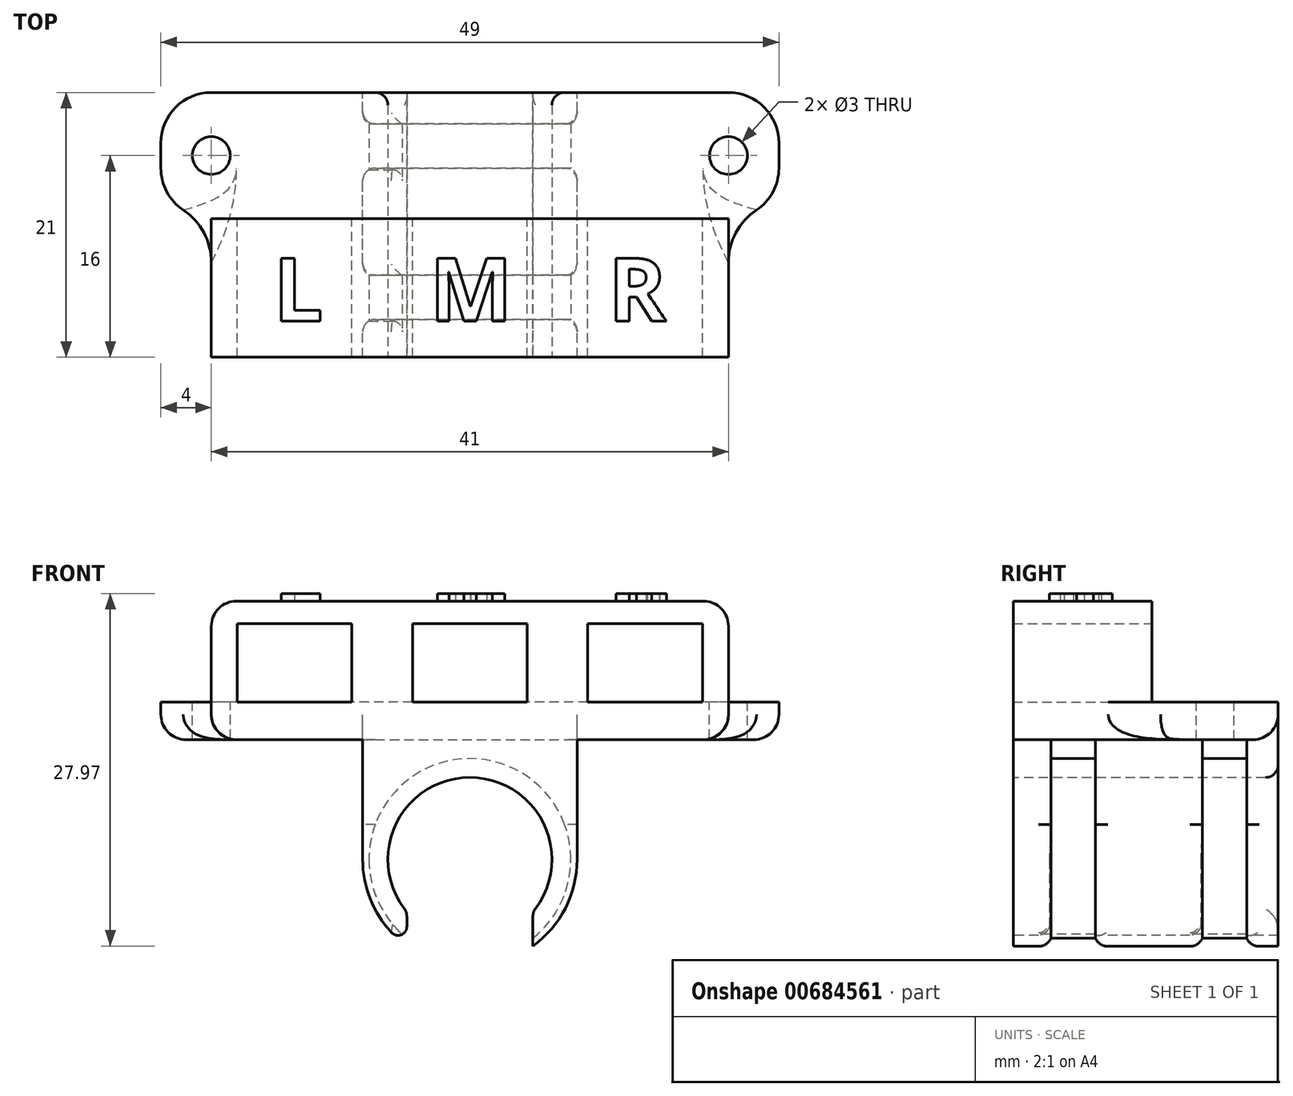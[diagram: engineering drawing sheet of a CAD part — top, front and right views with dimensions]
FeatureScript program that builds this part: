
annotation { "Feature Type Name" : "Feature", "Feature Type Description" : "" }
export const myFeature = defineFeature(function(context is Context, id is Id, definition is map)
    precondition{}
    {
        {
            var Q0;
            Q0=qCreatedBy(makeId("Front.planeOp"),FACE);
            var sketch = newSketch(context, id + "F0", { "sketchPlane" : qUnion([Q0])});
            skLineSegment(sketch, "E0.bottom", {"start": v(0, 0) * mm, "end": v(41, 0) * mm});
            skLineSegment(sketch, "E0.top", {"start": v(0, 11) * mm, "end": v(41, 11) * mm});
            skLineSegment(sketch, "E0.left", {"start": v(0, 0) * mm, "end": v(0, 11) * mm});
            skLineSegment(sketch, "E0.right", {"start": v(41, 0) * mm, "end": v(41, 11) * mm});
            skSolve(sketch);
        }
        {
            var Q0;
            Q0=makeQuery(id+"F0.imprint","IMPRINT",FACE,{"disambiguationData":[TD([[makeQuery(id+"F0.imprint","IMPRINT",EDGE,{"derivedFrom":sQuery(id+"F0.wireOp",EDGE,"E0.bottom")}),1.0]])]});
            extrude(context, id + "F1", {"entities" : qUnion([Q0]), "depth" : 11 * mm});
        }
        {
            var Q0;
            Q0=makeQuery(id+"F1.opExtrude","CAP_FACE",FACE,{"disambiguationData":[OSD([sQuery(id+"F0.wireOp",EDGE,"E0.bottom"),sQuery(id+"F0.wireOp",EDGE,"E0.top"),sQuery(id+"F0.wireOp",EDGE,"E0.left"),sQuery(id+"F0.wireOp",EDGE,"E0.right")])],"isStart":true});
            var sketch = newSketch(context, id + "F2", { "sketchPlane" : qUnion([Q0])});
            skLineSegment(sketch, "E1.bottom", {"start": v(-41, 0) * mm, "end": v(0, 0) * mm});
            skLineSegment(sketch, "E1.top", {"start": v(-41, 3) * mm, "end": v(0, 3) * mm});
            skLineSegment(sketch, "E1.left", {"start": v(-41, 0) * mm, "end": v(-41, 3) * mm});
            skLineSegment(sketch, "E1.right", {"start": v(0, 0) * mm, "end": v(0, 3) * mm});
            skSolve(sketch);
        }
        {
            var Q0;
            Q0=makeQuery(id+"F2.imprint","IMPRINT",FACE,{"disambiguationData":[TD([[makeQuery(id+"F2.imprint","IMPRINT",EDGE,{"derivedFrom":sQuery(id+"F2.wireOp",EDGE,"E1.bottom")}),-1.0]])]});
            extrude(context, id + "F3", {"entities" : qUnion([Q0]), "operationType" : NewBodyOperationType.ADD, "depth" : 10 * mm});
        }
        {
            var Q0;
            Q0=makeQuery(id+"F1.opExtrude","CAP_FACE",FACE,{"disambiguationData":[OSD([sQuery(id+"F0.wireOp",EDGE,"E0.bottom"),sQuery(id+"F0.wireOp",EDGE,"E0.top"),sQuery(id+"F0.wireOp",EDGE,"E0.left"),sQuery(id+"F0.wireOp",EDGE,"E0.right")])],"isStart":true});
            var sketch = newSketch(context, id + "F4", { "sketchPlane" : qUnion([Q0])});
            skLineSegment(sketch, "E2.bottom", {"start": v(-38.95, 3) * mm, "end": v(-29.85, 3) * mm});
            skLineSegment(sketch, "E2.top", {"start": v(-38.95, 9.2) * mm, "end": v(-29.85, 9.2) * mm});
            skLineSegment(sketch, "E2.left", {"start": v(-38.95, 3) * mm, "end": v(-38.95, 9.2) * mm});
            skLineSegment(sketch, "E2.right", {"start": v(-29.85, 3) * mm, "end": v(-29.85, 9.2) * mm});
            skLineSegment(sketch, "E3.bottom", {"start": v(-25.05, 3) * mm, "end": v(-15.95, 3) * mm});
            skLineSegment(sketch, "E3.top", {"start": v(-25.05, 9.2) * mm, "end": v(-15.95, 9.2) * mm});
            skLineSegment(sketch, "E3.left", {"start": v(-25.05, 3) * mm, "end": v(-25.05, 9.2) * mm});
            skLineSegment(sketch, "E3.right", {"start": v(-15.95, 3) * mm, "end": v(-15.95, 9.2) * mm});
            skLineSegment(sketch, "E4.bottom", {"start": v(-11.15, 3) * mm, "end": v(-2.05, 3) * mm});
            skLineSegment(sketch, "E4.top", {"start": v(-11.15, 9.2) * mm, "end": v(-2.05, 9.2) * mm});
            skLineSegment(sketch, "E4.left", {"start": v(-11.15, 3) * mm, "end": v(-11.15, 9.2) * mm});
            skLineSegment(sketch, "E4.right", {"start": v(-2.05, 3) * mm, "end": v(-2.05, 9.2) * mm});
            skSolve(sketch);
        }
        {
            var Q0;
            Q0=makeQuery(id+"F4.imprint","IMPRINT",FACE,{"disambiguationData":[TD([[makeQuery(id+"F4.imprint","IMPRINT",EDGE,{"derivedFrom":sQuery(id+"F4.wireOp",EDGE,"E2.bottom")}),1.0]])]});
            var Q1;
            Q1=makeQuery(id+"F4.imprint","IMPRINT",FACE,{"disambiguationData":[TD([[makeQuery(id+"F4.imprint","IMPRINT",EDGE,{"derivedFrom":sQuery(id+"F4.wireOp",EDGE,"E3.bottom")}),1.0]])]});
            var Q2;
            Q2=makeQuery(id+"F4.imprint","IMPRINT",FACE,{"disambiguationData":[TD([[makeQuery(id+"F4.imprint","IMPRINT",EDGE,{"derivedFrom":sQuery(id+"F4.wireOp",EDGE,"E4.bottom")}),1.0]])]});
            extrude(context, id + "F5", {"entities" : qUnion([Q0, Q1, Q2]), "operationType" : NewBodyOperationType.REMOVE, "endBound" : BoundingType.THROUGH_ALL, "oppositeDirection" : true, "depth" : 25 * mm});
        }
        {
            var Q0;
            Q0=makeQuery(id+"F3.boolean.opBoolean","MERGE",FACE,{"derivedFrom":[makeQuery(id+"F1.opExtrude","SWEPT_FACE",FACE,{"disambiguationData":[OSD([sQuery(id+"F0.wireOp",EDGE,"E0.bottom")])]}),makeQuery(id+"F3.opExtrude","SWEPT_FACE",FACE,{"disambiguationData":[OSD([sQuery(id+"F2.wireOp",EDGE,"E1.bottom")])]})]});
            var sketch = newSketch(context, id + "F6", { "sketchPlane" : qUnion([Q0])});
            skLineSegment(sketch, "E5.bottom", {"start": v(12, 11) * mm, "end": v(29, 11) * mm});
            skLineSegment(sketch, "E5.top", {"start": v(12, -10) * mm, "end": v(29, -10) * mm});
            skLineSegment(sketch, "E5.left", {"start": v(12, 11) * mm, "end": v(12, -10) * mm});
            skLineSegment(sketch, "E5.right", {"start": v(29, 11) * mm, "end": v(29, -10) * mm});
            skSolve(sketch);
        }
        {
            var Q0;
            Q0=makeQuery(id+"F6.imprint","IMPRINT",FACE,{"disambiguationData":[TD([[makeQuery(id+"F6.imprint","IMPRINT",EDGE,{"derivedFrom":sQuery(id+"F6.wireOp",EDGE,"E5.bottom")}),-1.0]])]});
            extrude(context, id + "F7", {"entities" : qUnion([Q0]), "operationType" : NewBodyOperationType.ADD, "depth" : 18 * mm});
        }
        {
            var Q0;
            Q0=makeQuery(id+"F7.opExtrude","CAP_EDGE",EDGE,{"disambiguationData":[OSD([sQuery(id+"F6.wireOp",EDGE,"E5.left")])],"isStart":false});
            var Q1;
            Q1=makeQuery(id+"F7.opExtrude","CAP_EDGE",EDGE,{"disambiguationData":[OSD([sQuery(id+"F6.wireOp",EDGE,"E5.right")])],"isStart":false});
            fillet(context, id + "F8", {"entities" : qUnion([Q0, Q1]), "radius" : 8.5 * mm, "tangentPropagation" : true, "allowEdgeOverflow" : false});
        }
        {
            var Q0;
            Q0=makeQuery(id+"F7.boolean.opBoolean","MERGE",FACE,{"derivedFrom":[makeQuery(id+"F1.opExtrude","CAP_FACE",FACE,{"disambiguationData":[OSD([sQuery(id+"F0.wireOp",EDGE,"E0.bottom"),sQuery(id+"F0.wireOp",EDGE,"E0.top"),sQuery(id+"F0.wireOp",EDGE,"E0.left"),sQuery(id+"F0.wireOp",EDGE,"E0.right")])],"isStart":false}),makeQuery(id+"F7.opExtrude","SWEPT_FACE",FACE,{"disambiguationData":[OSD([sQuery(id+"F6.wireOp",EDGE,"E5.bottom")])]})]});
            var sketch = newSketch(context, id + "F9", { "sketchPlane" : qUnion([Q0])});
            skCircle(sketch, "E6", {"center": v(20.5, -9.5) * mm, "radius": 6.5 * mm});
            skLineSegment(sketch, "E7.bottom", {"start": v(15.5, -10.8) * mm, "end": v(25.5, -10.8) * mm});
            skLineSegment(sketch, "E7.top", {"start": v(15.5, -21.95) * mm, "end": v(25.5, -21.95) * mm});
            skLineSegment(sketch, "E7.left", {"start": v(15.5, -10.8) * mm, "end": v(15.5, -21.95) * mm});
            skLineSegment(sketch, "E7.right", {"start": v(25.5, -10.8) * mm, "end": v(25.5, -21.95) * mm});
            skSolve(sketch);
        }
        {
            var Q0;
            {var subQ5=sQuery(id+"F9.wireOp",EDGE,"E7.bottom");Q0=makeQuery(id+"F9.imprint","IMPRINT",FACE,{"disambiguationData":[TD([[makeQuery(id+"F9.imprint","IMPRINT",EDGE,{"derivedFrom":subQ5}),1.0]])]});}
            var Q1;
            {var subQ5=sQuery(id+"F9.wireOp",EDGE,"E7.bottom");Q1=makeQuery(id+"F9.imprint","IMPRINT",FACE,{"disambiguationData":[TD([[makeQuery(id+"F9.imprint","IMPRINT",EDGE,{"derivedFrom":subQ5}),-1.0]])]});}
            var Q2;
            {var subQ0=sQuery(id+"F9.wireOp",EDGE,"E7.left");var subQ1=sQuery(id+"F9.wireOp",EDGE,"E6");var subQ2=makeQuery(id+"F9.imprint","INTERSECT",VERTEX,{"derivedFrom":[subQ1,subQ0]});Q2=makeQuery(id+"F9.imprint","IMPRINT",FACE,{"disambiguationData":[TD([[makeQuery(id+"F9.imprint","IMPRINT",EDGE,{"disambiguationData":[TD([[subQ2,-1.0]])],"derivedFrom":subQ1}),-1.0]])]});}
            extrude(context, id + "F10", {"entities" : qUnion([Q0, Q1, Q2]), "operationType" : NewBodyOperationType.REMOVE, "endBound" : BoundingType.THROUGH_ALL, "oppositeDirection" : true, "depth" : 25 * mm});
        }
        {
            var Q0;
            Q0=makeQuery(id+"F10.boolean.opBoolean","COPY",EDGE,{"derivedFrom":makeQuery(id+"F10.opExtrude","SWEPT_EDGE",EDGE,{"disambiguationData":[OSD([sQuery(id+"F0.wireOp",EDGE,"E0.bottom"),sQuery(id+"F0.wireOp",EDGE,"E0.top"),sQuery(id+"F0.wireOp",EDGE,"E0.left"),sQuery(id+"F0.wireOp",EDGE,"E0.right"),sQuery(id+"F6.wireOp",EDGE,"E5.bottom"),sQuery(id+"F6.wireOp",EDGE,"E5.right"),sQuery(id+"F9.wireOp",EDGE,"E7.left")])]})});
            var Q1;
            Q1=makeQuery(id+"F10.boolean.opBoolean","COPY",EDGE,{"derivedFrom":makeQuery(id+"F10.opExtrude","SWEPT_EDGE",EDGE,{"disambiguationData":[OSD([sQuery(id+"F0.wireOp",EDGE,"E0.bottom"),sQuery(id+"F0.wireOp",EDGE,"E0.top"),sQuery(id+"F0.wireOp",EDGE,"E0.left"),sQuery(id+"F0.wireOp",EDGE,"E0.right"),sQuery(id+"F6.wireOp",EDGE,"E5.bottom"),sQuery(id+"F6.wireOp",EDGE,"E5.right"),sQuery(id+"F9.wireOp",EDGE,"E7.right")])]})});
            fillet(context, id + "F11", {"entities" : qUnion([Q0, Q1]), "radius" : 0.7 * mm, "tangentPropagation" : true, "allowEdgeOverflow" : false});
        }
        {
            var Q0;
            Q0=qCreatedBy(makeId("Front.planeOp"),FACE);
            cPlane(context, id + "F12", {"entities" : qUnion([Q0]), "cplaneType" : CPlaneType.OFFSET, "offset" : 4 * mm, "oppositeDirection" : true, "width" : 150 * mm, "height" : 150 * mm});
        }
        {
            var Q0;
            Q0=qCreatedBy(makeId("Front.planeOp"),FACE);
            cPlane(context, id + "F13", {"entities" : qUnion([Q0]), "cplaneType" : CPlaneType.OFFSET, "offset" : 8 * mm, "width" : 150 * mm, "height" : 150 * mm});
        }
        {
            var Q0;
            Q0=qCreatedBy(id+"F13.planeOp",FACE);
            var sketch = newSketch(context, id + "F14", { "sketchPlane" : qUnion([Q0])});
            skLineSegment(sketch, "E8.bottom", {"start": v(0, 0) * mm, "end": v(41, 0) * mm});
            skLineSegment(sketch, "E8.top", {"start": v(0, -18) * mm, "end": v(41, -18) * mm});
            skLineSegment(sketch, "E8.left", {"start": v(0, 0) * mm, "end": v(0, -18) * mm});
            skLineSegment(sketch, "E8.right", {"start": v(41, 0) * mm, "end": v(41, -18) * mm});
            skCircle(sketch, "E9", {"center": v(20.5, -9.5) * mm, "radius": 8 * mm});
            skSolve(sketch);
        }
        {
            var Q0;
            Q0=makeQuery(id+"F14.imprint","IMPRINT",FACE,{"disambiguationData":[TD([[makeQuery(id+"F14.imprint","IMPRINT",EDGE,{"derivedFrom":sQuery(id+"F14.wireOp",EDGE,"E8.bottom")}),-1.0]])]});
            extrude(context, id + "F15", {"entities" : qUnion([Q0]), "operationType" : NewBodyOperationType.REMOVE, "oppositeDirection" : true, "depth" : 3.5 * mm});
        }
        {
            var Q0;
            Q0=qCreatedBy(id+"F12.planeOp",FACE);
            var sketch = newSketch(context, id + "F16", { "sketchPlane" : qUnion([Q0])});
            skLineSegment(sketch, "E10.bottom", {"start": v(0, 0) * mm, "end": v(41, 0) * mm});
            skLineSegment(sketch, "E10.top", {"start": v(0, -18) * mm, "end": v(41, -18) * mm});
            skLineSegment(sketch, "E10.left", {"start": v(0, 0) * mm, "end": v(0, -18) * mm});
            skLineSegment(sketch, "E10.right", {"start": v(41, 0) * mm, "end": v(41, -18) * mm});
            skCircle(sketch, "E11", {"center": v(20.5, -9.5) * mm, "radius": 8 * mm});
            skSolve(sketch);
        }
        {
            var Q0;
            Q0=makeQuery(id+"F16.imprint","IMPRINT",FACE,{"disambiguationData":[TD([[makeQuery(id+"F16.imprint","IMPRINT",EDGE,{"derivedFrom":sQuery(id+"F16.wireOp",EDGE,"E10.bottom")}),-1.0]])]});
            extrude(context, id + "F17", {"entities" : qUnion([Q0]), "operationType" : NewBodyOperationType.REMOVE, "oppositeDirection" : true, "depth" : 3.5 * mm});
        }
        {
            var Q0;
            Q0=makeQuery(id+"F15.boolean.opBoolean","INTERSECT",EDGE,{"derivedFrom":[makeQuery(id+"F7.opExtrude","SWEPT_FACE",FACE,{"disambiguationData":[OSD([sQuery(id+"F6.wireOp",EDGE,"E5.right")])]}),makeQuery(id+"F15.opExtrude","CAP_FACE",FACE,{"disambiguationData":[OSD([sQuery(id+"F14.wireOp",EDGE,"E8.bottom"),sQuery(id+"F14.wireOp",EDGE,"E8.top"),sQuery(id+"F14.wireOp",EDGE,"E8.left"),sQuery(id+"F14.wireOp",EDGE,"E8.right"),sQuery(id+"F14.wireOp",EDGE,"E9")])],"isStart":true})]});
            var Q1;
            Q1=makeQuery(id+"F15.boolean.opBoolean","INTERSECT",EDGE,{"derivedFrom":[makeQuery(id+"F7.opExtrude","SWEPT_FACE",FACE,{"disambiguationData":[OSD([sQuery(id+"F6.wireOp",EDGE,"E5.right")])]}),makeQuery(id+"F15.opExtrude","CAP_FACE",FACE,{"disambiguationData":[OSD([sQuery(id+"F14.wireOp",EDGE,"E8.bottom"),sQuery(id+"F14.wireOp",EDGE,"E8.top"),sQuery(id+"F14.wireOp",EDGE,"E8.left"),sQuery(id+"F14.wireOp",EDGE,"E8.right"),sQuery(id+"F14.wireOp",EDGE,"E9")])],"isStart":false})]});
            var Q2;
            {var subQ1=sQuery(id+"F6.wireOp",EDGE,"E5.right");Q2=makeQuery(id+"F17.boolean.opBoolean","INTERSECT",EDGE,{"derivedFrom":[makeQuery(id+"F15.boolean.opBoolean","SPLIT",FACE,{"disambiguationData":[TD([makeQuery(id+"F7.opExtrude","SWEPT_FACE",FACE,{"disambiguationData":[OSD([sQuery(id+"F6.wireOp",EDGE,"E5.top")])]})])],"derivedFrom":makeQuery(id+"F7.opExtrude","SWEPT_FACE",FACE,{"disambiguationData":[OSD([subQ1])]})}),makeQuery(id+"F17.opExtrude","CAP_FACE",FACE,{"disambiguationData":[OSD([sQuery(id+"F16.wireOp",EDGE,"E10.bottom"),sQuery(id+"F16.wireOp",EDGE,"E10.top"),sQuery(id+"F16.wireOp",EDGE,"E10.left"),sQuery(id+"F16.wireOp",EDGE,"E10.right"),sQuery(id+"F16.wireOp",EDGE,"E11")])],"isStart":true})]});}
            var Q3;
            {var subQ1=sQuery(id+"F6.wireOp",EDGE,"E5.right");Q3=makeQuery(id+"F17.boolean.opBoolean","INTERSECT",EDGE,{"derivedFrom":[makeQuery(id+"F15.boolean.opBoolean","SPLIT",FACE,{"disambiguationData":[TD([makeQuery(id+"F7.opExtrude","SWEPT_FACE",FACE,{"disambiguationData":[OSD([sQuery(id+"F6.wireOp",EDGE,"E5.top")])]})])],"derivedFrom":makeQuery(id+"F7.opExtrude","SWEPT_FACE",FACE,{"disambiguationData":[OSD([subQ1])]})}),makeQuery(id+"F17.opExtrude","CAP_FACE",FACE,{"disambiguationData":[OSD([sQuery(id+"F16.wireOp",EDGE,"E10.bottom"),sQuery(id+"F16.wireOp",EDGE,"E10.top"),sQuery(id+"F16.wireOp",EDGE,"E10.left"),sQuery(id+"F16.wireOp",EDGE,"E10.right"),sQuery(id+"F16.wireOp",EDGE,"E11")])],"isStart":false})]});}
            var Q4;
            Q4=makeQuery(id+"F15.boolean.opBoolean","INTERSECT",EDGE,{"derivedFrom":[makeQuery(id+"F7.opExtrude","SWEPT_FACE",FACE,{"disambiguationData":[OSD([sQuery(id+"F6.wireOp",EDGE,"E5.left")])]}),makeQuery(id+"F15.opExtrude","CAP_FACE",FACE,{"disambiguationData":[OSD([sQuery(id+"F14.wireOp",EDGE,"E8.bottom"),sQuery(id+"F14.wireOp",EDGE,"E8.top"),sQuery(id+"F14.wireOp",EDGE,"E8.left"),sQuery(id+"F14.wireOp",EDGE,"E8.right"),sQuery(id+"F14.wireOp",EDGE,"E9")])],"isStart":true})]});
            var Q5;
            Q5=makeQuery(id+"F15.boolean.opBoolean","INTERSECT",EDGE,{"derivedFrom":[makeQuery(id+"F7.opExtrude","SWEPT_FACE",FACE,{"disambiguationData":[OSD([sQuery(id+"F6.wireOp",EDGE,"E5.left")])]}),makeQuery(id+"F15.opExtrude","CAP_FACE",FACE,{"disambiguationData":[OSD([sQuery(id+"F14.wireOp",EDGE,"E8.bottom"),sQuery(id+"F14.wireOp",EDGE,"E8.top"),sQuery(id+"F14.wireOp",EDGE,"E8.left"),sQuery(id+"F14.wireOp",EDGE,"E8.right"),sQuery(id+"F14.wireOp",EDGE,"E9")])],"isStart":false})]});
            var Q6;
            Q6=makeQuery(id+"F17.boolean.opBoolean","INTERSECT",EDGE,{"derivedFrom":[makeQuery(id+"F15.boolean.opBoolean","SPLIT",FACE,{"disambiguationData":[TD([makeQuery(id+"F7.opExtrude","SWEPT_FACE",FACE,{"disambiguationData":[OSD([sQuery(id+"F6.wireOp",EDGE,"E5.top")])]})])],"derivedFrom":makeQuery(id+"F7.opExtrude","SWEPT_FACE",FACE,{"disambiguationData":[OSD([sQuery(id+"F6.wireOp",EDGE,"E5.left")])]})}),makeQuery(id+"F17.opExtrude","CAP_FACE",FACE,{"disambiguationData":[OSD([sQuery(id+"F16.wireOp",EDGE,"E10.bottom"),sQuery(id+"F16.wireOp",EDGE,"E10.top"),sQuery(id+"F16.wireOp",EDGE,"E10.left"),sQuery(id+"F16.wireOp",EDGE,"E10.right"),sQuery(id+"F16.wireOp",EDGE,"E11")])],"isStart":true})]});
            var Q7;
            Q7=makeQuery(id+"F17.boolean.opBoolean","INTERSECT",EDGE,{"derivedFrom":[makeQuery(id+"F15.boolean.opBoolean","SPLIT",FACE,{"disambiguationData":[TD([makeQuery(id+"F7.opExtrude","SWEPT_FACE",FACE,{"disambiguationData":[OSD([sQuery(id+"F6.wireOp",EDGE,"E5.top")])]})])],"derivedFrom":makeQuery(id+"F7.opExtrude","SWEPT_FACE",FACE,{"disambiguationData":[OSD([sQuery(id+"F6.wireOp",EDGE,"E5.left")])]})}),makeQuery(id+"F17.opExtrude","CAP_FACE",FACE,{"disambiguationData":[OSD([sQuery(id+"F16.wireOp",EDGE,"E10.bottom"),sQuery(id+"F16.wireOp",EDGE,"E10.top"),sQuery(id+"F16.wireOp",EDGE,"E10.left"),sQuery(id+"F16.wireOp",EDGE,"E10.right"),sQuery(id+"F16.wireOp",EDGE,"E11")])],"isStart":false})]});
            fillet(context, id + "F18", {"entities" : qUnion([Q0, Q1, Q2, Q3, Q4, Q5, Q6, Q7]), "radius" : 1 * mm, "tangentPropagation" : true, "allowEdgeOverflow" : false});
        }
        {
            var Q0;
            Q0=makeQuery(id+"F3.boolean.opBoolean","MERGE",FACE,{"derivedFrom":[makeQuery(id+"F1.opExtrude","SWEPT_FACE",FACE,{"disambiguationData":[OSD([sQuery(id+"F0.wireOp",EDGE,"E0.left")])]}),makeQuery(id+"F3.opExtrude","SWEPT_FACE",FACE,{"disambiguationData":[OSD([sQuery(id+"F2.wireOp",EDGE,"E1.right")])]})]});
            var sketch = newSketch(context, id + "F19", { "sketchPlane" : qUnion([Q0])});
            skLineSegment(sketch, "E12.bottom", {"start": v(0, 3) * mm, "end": v(-10, 3) * mm});
            skLineSegment(sketch, "E12.top", {"start": v(0, 0) * mm, "end": v(-10, 0) * mm});
            skLineSegment(sketch, "E12.left", {"start": v(0, 3) * mm, "end": v(0, 0) * mm});
            skLineSegment(sketch, "E12.right", {"start": v(-10, 3) * mm, "end": v(-10, 0) * mm});
            skSolve(sketch);
        }
        {
            var Q0;
            Q0=makeQuery(id+"F19.imprint","IMPRINT",FACE,{"disambiguationData":[TD([[makeQuery(id+"F19.imprint","IMPRINT",EDGE,{"derivedFrom":sQuery(id+"F19.wireOp",EDGE,"E12.bottom")}),-1.0]])]});
            extrude(context, id + "F20", {"entities" : qUnion([Q0]), "operationType" : NewBodyOperationType.ADD, "depth" : 4 * mm});
        }
        {
            var Q0;
            Q0=makeQuery(id+"F3.boolean.opBoolean","MERGE",FACE,{"derivedFrom":[makeQuery(id+"F1.opExtrude","SWEPT_FACE",FACE,{"disambiguationData":[OSD([sQuery(id+"F0.wireOp",EDGE,"E0.right")])]}),makeQuery(id+"F3.opExtrude","SWEPT_FACE",FACE,{"disambiguationData":[OSD([sQuery(id+"F2.wireOp",EDGE,"E1.left")])]})]});
            var sketch = newSketch(context, id + "F21", { "sketchPlane" : qUnion([Q0])});
            skLineSegment(sketch, "E13.bottom", {"start": v(0, 3) * mm, "end": v(10, 3) * mm});
            skLineSegment(sketch, "E13.top", {"start": v(0, 0) * mm, "end": v(10, 0) * mm});
            skLineSegment(sketch, "E13.left", {"start": v(0, 3) * mm, "end": v(0, 0) * mm});
            skLineSegment(sketch, "E13.right", {"start": v(10, 3) * mm, "end": v(10, 0) * mm});
            skSolve(sketch);
        }
        {
            var Q0;
            Q0=makeQuery(id+"F21.imprint","IMPRINT",FACE,{"disambiguationData":[TD([[makeQuery(id+"F21.imprint","IMPRINT",EDGE,{"derivedFrom":sQuery(id+"F21.wireOp",EDGE,"E13.bottom")}),1.0]])]});
            extrude(context, id + "F22", {"entities" : qUnion([Q0]), "operationType" : NewBodyOperationType.ADD, "depth" : 4 * mm});
        }
        {
            var Q0;
            Q0=makeQuery(id+"F22.opExtrude","CAP_EDGE",EDGE,{"disambiguationData":[OSD([sQuery(id+"F21.wireOp",EDGE,"E13.left")])],"isStart":false});
            var Q1;
            Q1=makeQuery(id+"F22.opExtrude","CAP_EDGE",EDGE,{"disambiguationData":[OSD([sQuery(id+"F21.wireOp",EDGE,"E13.right")])],"isStart":false});
            var Q2;
            Q2=makeQuery(id+"F20.opExtrude","CAP_EDGE",EDGE,{"disambiguationData":[OSD([sQuery(id+"F19.wireOp",EDGE,"E12.right")])],"isStart":false});
            var Q3;
            Q3=makeQuery(id+"F20.opExtrude","CAP_EDGE",EDGE,{"disambiguationData":[OSD([sQuery(id+"F19.wireOp",EDGE,"E12.left")])],"isStart":false});
            fillet(context, id + "F23", {"entities" : qUnion([Q0, Q1, Q2, Q3]), "radius" : 4 * mm, "tangentPropagation" : true, "allowEdgeOverflow" : false});
        }
        {
            var Q0;
            Q0=makeQuery(id+"F1.opExtrude","SWEPT_EDGE",EDGE,{"disambiguationData":[OSD([sQuery(id+"F0.wireOp",EDGE,"E0.top"),sQuery(id+"F0.wireOp",EDGE,"E0.left")])]});
            var Q1;
            Q1=makeQuery(id+"F3.boolean.opBoolean","MERGE",EDGE,{"derivedFrom":[makeQuery(id+"F1.opExtrude","SWEPT_EDGE",EDGE,{"disambiguationData":[OSD([sQuery(id+"F0.wireOp",EDGE,"E0.bottom"),sQuery(id+"F0.wireOp",EDGE,"E0.left")])]}),makeQuery(id+"F3.opExtrude","SWEPT_EDGE",EDGE,{"disambiguationData":[OSD([sQuery(id+"F2.wireOp",EDGE,"E1.bottom"),sQuery(id+"F2.wireOp",EDGE,"E1.right")])]})]});
            var Q2;
            Q2=makeQuery(id+"F3.boolean.opBoolean","MERGE",EDGE,{"derivedFrom":[makeQuery(id+"F1.opExtrude","SWEPT_EDGE",EDGE,{"disambiguationData":[OSD([sQuery(id+"F0.wireOp",EDGE,"E0.bottom"),sQuery(id+"F0.wireOp",EDGE,"E0.right")])]}),makeQuery(id+"F3.opExtrude","SWEPT_EDGE",EDGE,{"disambiguationData":[OSD([sQuery(id+"F2.wireOp",EDGE,"E1.bottom"),sQuery(id+"F2.wireOp",EDGE,"E1.left")])]})]});
            var Q3;
            {var subQ2=sQuery(id+"F2.wireOp",EDGE,"E1.bottom");var subQ4=sQuery(id+"F0.wireOp",EDGE,"E0.right");var subQ5=sQuery(id+"F0.wireOp",EDGE,"E0.left");var subQ6=sQuery(id+"F0.wireOp",EDGE,"E0.bottom");var subQ10=makeQuery(id+"F3.boolean.opBoolean","MERGE",FACE,{"derivedFrom":[makeQuery(id+"F1.opExtrude","SWEPT_FACE",FACE,{"disambiguationData":[OSD([subQ6])]}),makeQuery(id+"F3.opExtrude","SWEPT_FACE",FACE,{"disambiguationData":[OSD([subQ2])]})]});Q3=makeQuery(id+"F23.opFillet","BLEND_EDGE",EDGE,{"blendedFrom":[makeQuery(id+"F22.opExtrude","CAP_EDGE",EDGE,{"disambiguationData":[OSD([sQuery(id+"F21.wireOp",EDGE,"E13.left")])],"isStart":false}),makeQuery(id+"F22.boolean.opBoolean","MERGE",FACE,{"derivedFrom":[makeQuery(id+"F20.boolean.opBoolean","MERGE",FACE,{"derivedFrom":[makeQuery(id+"F17.boolean.opBoolean","MERGE",FACE,{"derivedFrom":[makeQuery(id+"F15.boolean.opBoolean","MERGE",FACE,{"derivedFrom":[makeQuery(id+"F7.boolean.opBoolean","SPLIT",FACE,{"disambiguationData":[TD([makeQuery(id+"F1.opExtrude","SWEPT_FACE",FACE,{"disambiguationData":[OSD([subQ5])]})])],"derivedFrom":subQ10}),makeQuery(id+"F7.boolean.opBoolean","SPLIT",FACE,{"disambiguationData":[TD([makeQuery(id+"F1.opExtrude","SWEPT_FACE",FACE,{"disambiguationData":[OSD([subQ4])]})])],"derivedFrom":subQ10}),makeQuery(id+"F15.opExtrude","SWEPT_FACE",FACE,{"disambiguationData":[OSD([sQuery(id+"F14.wireOp",EDGE,"E8.bottom")])]})]}),makeQuery(id+"F17.opExtrude","SWEPT_FACE",FACE,{"disambiguationData":[OSD([sQuery(id+"F16.wireOp",EDGE,"E10.bottom")])]})]}),makeQuery(id+"F20.opExtrude","SWEPT_FACE",FACE,{"disambiguationData":[OSD([sQuery(id+"F19.wireOp",EDGE,"E12.top")])]})]}),makeQuery(id+"F22.opExtrude","SWEPT_FACE",FACE,{"disambiguationData":[OSD([sQuery(id+"F21.wireOp",EDGE,"E13.top")])]})]})],"blendedInto":[makeQuery(id+"F22.boolean.opBoolean","MERGE",FACE,{"derivedFrom":[makeQuery(id+"F20.boolean.opBoolean","MERGE",FACE,{"derivedFrom":[makeQuery(id+"F17.boolean.opBoolean","MERGE",FACE,{"derivedFrom":[makeQuery(id+"F15.boolean.opBoolean","MERGE",FACE,{"derivedFrom":[makeQuery(id+"F7.boolean.opBoolean","SPLIT",FACE,{"disambiguationData":[TD([makeQuery(id+"F1.opExtrude","SWEPT_FACE",FACE,{"disambiguationData":[OSD([subQ5])]})])],"derivedFrom":subQ10}),makeQuery(id+"F7.boolean.opBoolean","SPLIT",FACE,{"disambiguationData":[TD([makeQuery(id+"F1.opExtrude","SWEPT_FACE",FACE,{"disambiguationData":[OSD([subQ4])]})])],"derivedFrom":subQ10}),makeQuery(id+"F15.opExtrude","SWEPT_FACE",FACE,{"disambiguationData":[OSD([sQuery(id+"F14.wireOp",EDGE,"E8.bottom")])]})]}),makeQuery(id+"F17.opExtrude","SWEPT_FACE",FACE,{"disambiguationData":[OSD([sQuery(id+"F16.wireOp",EDGE,"E10.bottom")])]})]}),makeQuery(id+"F20.opExtrude","SWEPT_FACE",FACE,{"disambiguationData":[OSD([sQuery(id+"F19.wireOp",EDGE,"E12.top")])]})]}),makeQuery(id+"F22.opExtrude","SWEPT_FACE",FACE,{"disambiguationData":[OSD([sQuery(id+"F21.wireOp",EDGE,"E13.top")])]})]})]});}
            var Q4;
            {var subQ0=sQuery(id+"F2.wireOp",EDGE,"E1.bottom");Q4=makeQuery(id+"F20.boolean.opBoolean","MERGE",EDGE,{"derivedFrom":[makeQuery(id+"F7.boolean.opBoolean","SPLIT",EDGE,{"disambiguationData":[TD([makeQuery(id+"F1.opExtrude","SWEPT_FACE",FACE,{"disambiguationData":[OSD([sQuery(id+"F0.wireOp",EDGE,"E0.left")])]})])],"derivedFrom":makeQuery(id+"F3.opExtrude","CAP_EDGE",EDGE,{"disambiguationData":[OSD([subQ0])],"isStart":false})}),makeQuery(id+"F20.opExtrude","SWEPT_EDGE",EDGE,{"disambiguationData":[OSD([sQuery(id+"F19.wireOp",EDGE,"E12.top"),sQuery(id+"F19.wireOp",EDGE,"E12.right")])]})]});}
            var Q5;
            Q5=makeQuery(id+"F1.opExtrude","SWEPT_EDGE",EDGE,{"disambiguationData":[OSD([sQuery(id+"F0.wireOp",EDGE,"E0.top"),sQuery(id+"F0.wireOp",EDGE,"E0.right")])]});
            fillet(context, id + "F24", {"entities" : qUnion([Q0, Q1, Q2, Q3, Q4, Q5]), "radius" : 2 * mm, "tangentPropagation" : true, "allowEdgeOverflow" : false});
        }
        {
            var Q0;
            Q0=makeQuery(id+"F22.boolean.opBoolean","MERGE",FACE,{"derivedFrom":[makeQuery(id+"F20.boolean.opBoolean","MERGE",FACE,{"derivedFrom":[makeQuery(id+"F5.boolean.opBoolean","MERGE",FACE,{"derivedFrom":[makeQuery(id+"F3.opExtrude","SWEPT_FACE",FACE,{"disambiguationData":[OSD([sQuery(id+"F2.wireOp",EDGE,"E1.top")])]}),makeQuery(id+"F5.opExtrude","SWEPT_FACE",FACE,{"disambiguationData":[OSD([sQuery(id+"F4.wireOp",EDGE,"E2.bottom")])]}),makeQuery(id+"F5.opExtrude","SWEPT_FACE",FACE,{"disambiguationData":[OSD([sQuery(id+"F4.wireOp",EDGE,"E3.bottom")])]}),makeQuery(id+"F5.opExtrude","SWEPT_FACE",FACE,{"disambiguationData":[OSD([sQuery(id+"F4.wireOp",EDGE,"E4.bottom")])]})]}),makeQuery(id+"F20.opExtrude","SWEPT_FACE",FACE,{"disambiguationData":[OSD([sQuery(id+"F19.wireOp",EDGE,"E12.bottom")])]})]}),makeQuery(id+"F22.opExtrude","SWEPT_FACE",FACE,{"disambiguationData":[OSD([sQuery(id+"F21.wireOp",EDGE,"E13.bottom")])]})]});
            var sketch = newSketch(context, id + "F25", { "sketchPlane" : qUnion([Q0])});
            skCircle(sketch, "E14", {"center": v(0, 5) * mm, "radius": 1.5 * mm});
            skCircle(sketch, "E15", {"center": v(41, 5) * mm, "radius": 1.5 * mm});
            skSolve(sketch);
        }
        {
            var Q0;
            Q0=makeQuery(id+"F25.imprint","IMPRINT",FACE,{"disambiguationData":[TD([[makeQuery(id+"F25.imprint","IMPRINT",EDGE,{"derivedFrom":sQuery(id+"F25.wireOp",EDGE,"E15")}),1.0]])]});
            var Q1;
            Q1=makeQuery(id+"F25.imprint","IMPRINT",FACE,{"disambiguationData":[TD([[makeQuery(id+"F25.imprint","IMPRINT",EDGE,{"derivedFrom":sQuery(id+"F25.wireOp",EDGE,"E14")}),1.0]])]});
            extrude(context, id + "F26", {"entities" : qUnion([Q0, Q1]), "operationType" : NewBodyOperationType.REMOVE, "endBound" : BoundingType.THROUGH_ALL, "oppositeDirection" : true, "depth" : 25 * mm});
        }
        {
            var Q0;
            Q0=makeQuery(id+"F1.opExtrude","SWEPT_FACE",FACE,{"disambiguationData":[OSD([sQuery(id+"F0.wireOp",EDGE,"E0.top")])]});
            var sketch = newSketch(context, id + "F27", { "sketchPlane" : qUnion([Q0])});
            skText(sketch, "E16", { "text": "L", "fontName": "OpenSans-Bold.ttf"});
            skText(sketch, "E17", { "text": "M", "fontName": "OpenSans-Bold.ttf"});
            skText(sketch, "E18", { "text": "R", "fontName": "OpenSans-Bold.ttf"});
            const initialGuessF27  = {"E16": [0.00492, -0.00815, 1, 0, 0.00504], "E17": [0.01729, -0.00815, 1, 0, 0.00504], "E18": [0.03146, -0.00815, 1, 0, 0.00504]};
            skSetInitialGuess(sketch, initialGuessF27);
            skSolve(sketch);
        }
        {
            var Q0;
            Q0=makeQuery(id+"F27.imprint","IMPRINT",FACE,{"disambiguationData":[TD([[makeQuery(id+"F27.imprint","IMPRINT",EDGE,{"derivedFrom":sQuery(id+"F27.wireOp",EDGE,"E16.sketch_text.stroke-0")}),-1.0]])]});
            var Q1;
            Q1=makeQuery(id+"F27.imprint","IMPRINT",FACE,{"disambiguationData":[TD([[makeQuery(id+"F27.imprint","IMPRINT",EDGE,{"derivedFrom":sQuery(id+"F27.wireOp",EDGE,"E17.sketch_text.stroke-0")}),-1.0]])]});
            var Q2;
            Q2=makeQuery(id+"F27.imprint","IMPRINT",FACE,{"disambiguationData":[TD([[makeQuery(id+"F27.imprint","IMPRINT",EDGE,{"derivedFrom":sQuery(id+"F27.wireOp",EDGE,"E18.sketch_text.stroke-0")}),-1.0]])]});
            extrude(context, id + "F28", {"entities" : qUnion([Q0, Q1, Q2]), "operationType" : NewBodyOperationType.ADD, "depth" : 0.6 * mm});
        }
        {
            var Q0;
            Q0=makeQuery(id+"F10.boolean.opBoolean","COPY",EDGE,{"derivedFrom":makeQuery(id+"F10.opExtrude","CAP_EDGE",EDGE,{"disambiguationData":[OSD([sQuery(id+"F9.wireOp",EDGE,"E6")])],"isStart":true})});
            var Q1;
            Q1=makeQuery(id+"F10.boolean.opBoolean","INTERSECT",EDGE,{"derivedFrom":[makeQuery(id+"F7.boolean.opBoolean","MERGE",FACE,{"derivedFrom":[makeQuery(id+"F3.opExtrude","CAP_FACE",FACE,{"disambiguationData":[OSD([sQuery(id+"F2.wireOp",EDGE,"E1.bottom"),sQuery(id+"F2.wireOp",EDGE,"E1.top"),sQuery(id+"F2.wireOp",EDGE,"E1.left"),sQuery(id+"F2.wireOp",EDGE,"E1.right")])],"isStart":false}),makeQuery(id+"F7.opExtrude","SWEPT_FACE",FACE,{"disambiguationData":[OSD([sQuery(id+"F6.wireOp",EDGE,"E5.top")])]})]}),makeQuery(id+"F10.opExtrude","SWEPT_FACE",FACE,{"disambiguationData":[OSD([sQuery(id+"F9.wireOp",EDGE,"E6")])]})]});
            var Q2;
            Q2=makeQuery(id+"F10.boolean.opBoolean","COPY",EDGE,{"derivedFrom":makeQuery(id+"F10.opExtrude","SWEPT_EDGE",EDGE,{"disambiguationData":[OSD([sQuery(id+"F9.wireOp",EDGE,"E6"),sQuery(id+"F9.wireOp",EDGE,"E7.left")])]})});
            var Q3;
            Q3=makeQuery(id+"F10.boolean.opBoolean","COPY",EDGE,{"derivedFrom":makeQuery(id+"F10.opExtrude","SWEPT_EDGE",EDGE,{"disambiguationData":[OSD([sQuery(id+"F9.wireOp",EDGE,"E6"),sQuery(id+"F9.wireOp",EDGE,"E7.right")])]})});
            fillet(context, id + "F29", {"entities" : qUnion([Q0, Q1, Q2, Q3]), "radius" : 1 * mm, "tangentPropagation" : true, "allowEdgeOverflow" : false});
        }
        {
            var Q0;
            Q0=makeQuery(id+"F23.opFillet","BLEND_EDGE",EDGE,{"blendedFrom":[makeQuery(id+"F20.opExtrude","CAP_EDGE",EDGE,{"disambiguationData":[OSD([sQuery(id+"F19.wireOp",EDGE,"E12.left")])],"isStart":false}),makeQuery(id+"F3.boolean.opBoolean","MERGE",FACE,{"derivedFrom":[makeQuery(id+"F1.opExtrude","SWEPT_FACE",FACE,{"disambiguationData":[OSD([sQuery(id+"F0.wireOp",EDGE,"E0.left")])]}),makeQuery(id+"F3.opExtrude","SWEPT_FACE",FACE,{"disambiguationData":[OSD([sQuery(id+"F2.wireOp",EDGE,"E1.right")])]})]})],"blendedInto":[makeQuery(id+"F3.boolean.opBoolean","MERGE",FACE,{"derivedFrom":[makeQuery(id+"F1.opExtrude","SWEPT_FACE",FACE,{"disambiguationData":[OSD([sQuery(id+"F0.wireOp",EDGE,"E0.left")])]}),makeQuery(id+"F3.opExtrude","SWEPT_FACE",FACE,{"disambiguationData":[OSD([sQuery(id+"F2.wireOp",EDGE,"E1.right")])]})]})]});
            var Q1;
            Q1=makeQuery(id+"F23.opFillet","BLEND_EDGE",EDGE,{"blendedFrom":[makeQuery(id+"F22.opExtrude","CAP_EDGE",EDGE,{"disambiguationData":[OSD([sQuery(id+"F21.wireOp",EDGE,"E13.left")])],"isStart":false}),makeQuery(id+"F3.boolean.opBoolean","MERGE",FACE,{"derivedFrom":[makeQuery(id+"F1.opExtrude","SWEPT_FACE",FACE,{"disambiguationData":[OSD([sQuery(id+"F0.wireOp",EDGE,"E0.right")])]}),makeQuery(id+"F3.opExtrude","SWEPT_FACE",FACE,{"disambiguationData":[OSD([sQuery(id+"F2.wireOp",EDGE,"E1.left")])]})]})],"blendedInto":[makeQuery(id+"F3.boolean.opBoolean","MERGE",FACE,{"derivedFrom":[makeQuery(id+"F1.opExtrude","SWEPT_FACE",FACE,{"disambiguationData":[OSD([sQuery(id+"F0.wireOp",EDGE,"E0.right")])]}),makeQuery(id+"F3.opExtrude","SWEPT_FACE",FACE,{"disambiguationData":[OSD([sQuery(id+"F2.wireOp",EDGE,"E1.left")])]})]})]});
            fillet(context, id + "F30", {"entities" : qUnion([Q0, Q1]), "radius" : 5 * mm, "tangentPropagation" : true, "allowEdgeOverflow" : false});
        }
    });
